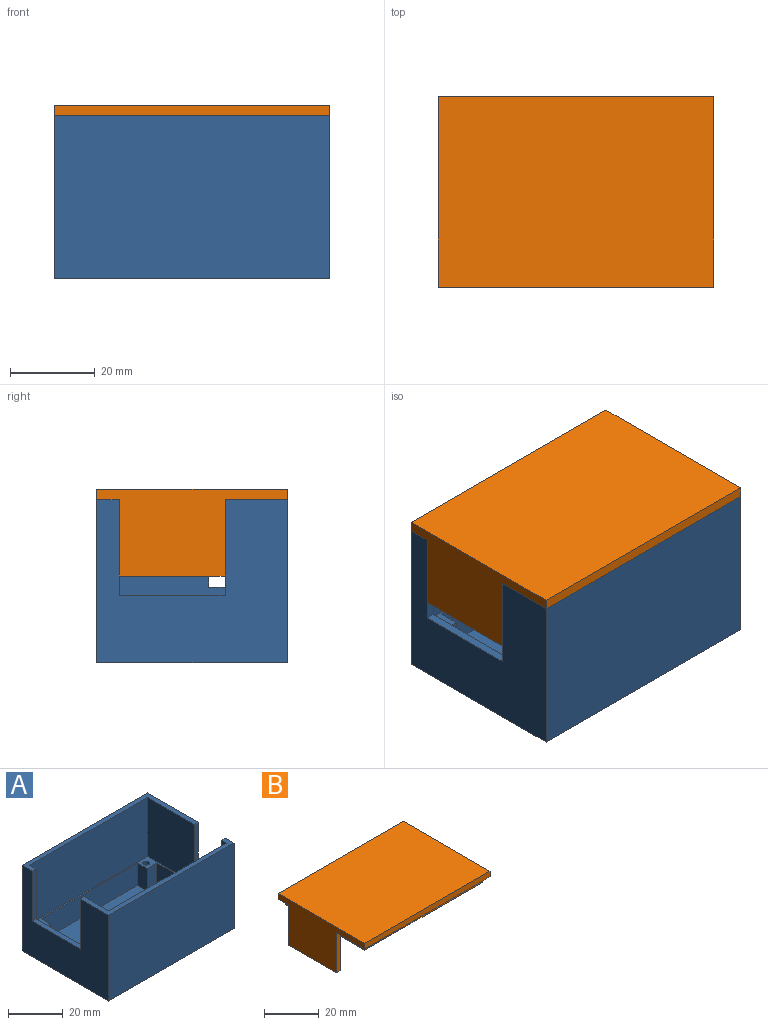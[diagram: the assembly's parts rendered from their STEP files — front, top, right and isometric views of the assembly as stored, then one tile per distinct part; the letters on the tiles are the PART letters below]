
ASSEMBLY  parts=2 mates=1
PART A: 39 faces, bbox 65x45x38.5 mm
  f0: plane 45x38.5mm, normal (-1,0,0), area 1170mm2, adj f1,f3,f4,f5,f10,f11,f14,f37
  f1: plane 65x38.5mm, normal (0,-1,0), area 2502.5mm2, adj f0,f2,f4,f14
  f2: plane 45x38.5mm, normal (1,0,0), area 1444.1mm2, adj f1,f3,f4,f9,f10,f12,f14,f38
  f3: plane 65x38.5mm, normal (0,1,0), area 2502.5mm2, adj f0,f2,f4,f10
  f4: plane 65x45mm, normal (0,0,-1), area 2925mm2, adj f0,f1,f2,f3
  f5: plane 22.5x2mm, normal (0,-1,0), area 45mm2, adj f0,f6,f10,f37
  f6: plane 41x26.5mm, normal (1,0,0), area 524mm2, adj f5,f7,f10,f11,f13,f14,f31,f37
  f7: plane 61x26.5mm, normal (0,-1,0), area 1616.5mm2, adj f6,f8,f10,f31
  f8: plane 41x26.5mm, normal (-1,0,0), area 798.1mm2, adj f7,f9,f10,f12,f13,f14,f31,f38
  f9: plane 20.6x2mm, normal (0,-1,0), area 41.2mm2, adj f2,f8,f10,f38
  f10: plane 65x26.5mm, normal (0,0,1), area 185.6mm2, adj f0,f2,f3,f5,f6,f7,f8,f9
  f11: plane 22.5x2mm, normal (0,1,0), area 45mm2, adj f0,f6,f14,f37
  f12: plane 20.6x2mm, normal (0,1,0), area 41.2mm2, adj f2,f8,f14,f38
  f13: plane 61x26.5mm, normal (0,1,0), area 1616.5mm2, adj f6,f8,f14,f31
  f14: plane 65x14.7mm, normal (0,0,1), area 160.4mm2, adj f0,f1,f2,f6,f8,f11,f12,f13
  f15: plane 10x5mm, normal (1,0,0), area 50mm2, adj f16,f30,f31,f36
  f16: plane 50x10mm, normal (0,-1,0), area 500mm2, adj f15,f17,f31,f36
  f17: plane 10x5mm, normal (-1,0,0), area 50mm2, adj f16,f18,f31,f36
  f18: plane 10x5mm, normal (0,-1,0), area 50mm2, adj f17,f19,f31,f36
  f19: plane 30x10mm, normal (-1,0,0), area 300mm2, adj f18,f20,f31,f36
  f20: plane 10x5mm, normal (0,1,0), area 50mm2, adj f19,f21,f31,f36
  f21: plane 10x5mm, normal (-1,0,0), area 50mm2, adj f20,f22,f31,f36
  f22: plane 50x10mm, normal (0,1,0), area 500mm2, adj f21,f23,f31,f36
  f23: plane 10x5mm, normal (1,0,0), area 50mm2, adj f22,f24,f31,f36
  f24: plane 10x5mm, normal (0,1,0), area 50mm2, adj f23,f25,f31,f36
  f25: plane 30x10mm, normal (1,0,0), area 300mm2, adj f24,f30,f31,f36
  f26: cylinder r=1.25mm len=10mm, axis (0,0,-1), area 78.5mm2, adj f31,f35
  f27: cylinder r=1.25mm len=10mm, axis (0,0,-1), area 78.5mm2, adj f31,f34
  f28: cylinder r=1.25mm len=10mm, axis (0,0,-1), area 78.5mm2, adj f31,f33
  f29: cylinder r=1.25mm len=10mm, axis (0,0,-1), area 78.5mm2, adj f31,f32
  f30: plane 10x5mm, normal (0,-1,0), area 50mm2, adj f15,f25,f31,f36
  f31: plane 61x41mm, normal (0,0,1), area 181.4mm2, adj f6,f7,f8,f13,f15,f16,f17,f18
  f32: plane 2.5x2.5mm, normal (0,0,1), area 4.9mm2, adj f29
  f33: plane 2.5x2.5mm, normal (0,0,1), area 4.9mm2, adj f28
  f34: plane 2.5x2.5mm, normal (0,0,1), area 4.9mm2, adj f27
  f35: plane 2.5x2.5mm, normal (0,0,1), area 4.9mm2, adj f26
  f36: plane 60x40mm, normal (0,0,1), area 2300mm2, adj f15,f16,f17,f18,f19,f20,f21,f22
  f37: plane 25x2mm, normal (0,0,1), area 50mm2, adj f0,f5,f6,f11
  f38: plane 14x2mm, normal (0,0,1), area 28mm2, adj f2,f8,f9,f12
PART B: 22 faces, bbox 65x45x20.5 mm
  f0: plane 65x14.7mm, normal (0,0,-1), area 160.4mm2, adj f4,f5,f6,f10,f11,f12,f16,f20
  f1: plane 3.3x2.5mm, normal (-1,0,0), area 8.2mm2, adj f2,f9,f13,f19
  f2: plane 65x26.5mm, normal (0,0,-1), area 185.6mm2, adj f1,f3,f4,f6,f7,f9,f15,f19
  f3: plane 24.5x2.5mm, normal (1,0,0), area 61.2mm2, adj f2,f9,f13,f15
  f4: plane 45x20.5mm, normal (-1,0,0), area 562.5mm2, adj f0,f2,f5,f7,f8,f19,f20,f21
  f5: plane 65x2.5mm, normal (0,-1,0), area 162.5mm2, adj f0,f4,f6,f8
  f6: plane 45x7.5mm, normal (1,0,0), area 182.5mm2, adj f0,f2,f5,f7,f8,f15,f16,f17
  f7: plane 65x2.5mm, normal (0,1,0), area 162.5mm2, adj f2,f4,f6,f8
  f8: plane 65x45mm, normal (0,0,1), area 2925mm2, adj f4,f5,f6,f7
  f9: plane 61x2.5mm, normal (0,1,0), area 152.5mm2, adj f1,f2,f3,f13
  f10: plane 12.7x2.5mm, normal (-1,0,0), area 31.8mm2, adj f0,f11,f13,f20
  f11: plane 61x2.5mm, normal (0,-1,0), area 152.5mm2, adj f0,f10,f12,f13
  f12: plane 2.5x2.5mm, normal (1,0,0), area 6.3mm2, adj f0,f11,f13,f16
  f13: plane 61x41mm, normal (0,0,-1), area 2501mm2, adj f1,f3,f9,f10,f11,f12,f14,f18
  f14: plane 14x2.5mm, normal (-1,0,0), area 35mm2, adj f13,f15,f16,f17
  f15: plane 5x2mm, normal (0,1,0), area 10mm2, adj f2,f3,f6,f14,f17
  f16: plane 5x2mm, normal (0,-1,0), area 10mm2, adj f0,f6,f12,f14,f17
  f17: plane 14x2mm, normal (0,0,-1), area 28mm2, adj f6,f14,f15,f16
  f18: plane 25x15.5mm, normal (1,0,0), area 387.5mm2, adj f13,f19,f20,f21
  f19: plane 18x2mm, normal (0,1,0), area 36mm2, adj f1,f2,f4,f18,f21
  f20: plane 18x2mm, normal (0,-1,0), area 36mm2, adj f0,f4,f10,f18,f21
  f21: plane 25x2mm, normal (0,0,-1), area 50mm2, adj f4,f18,f19,f20
PLACE A t=(113.55,65.46,-31.79)mm
PLACE B t=(113.55,65.46,4.71)mm
MATE fastened B.f0 <-> A.f14  axis (0,0,-1) through (109.54,45.19,4.71)mm
